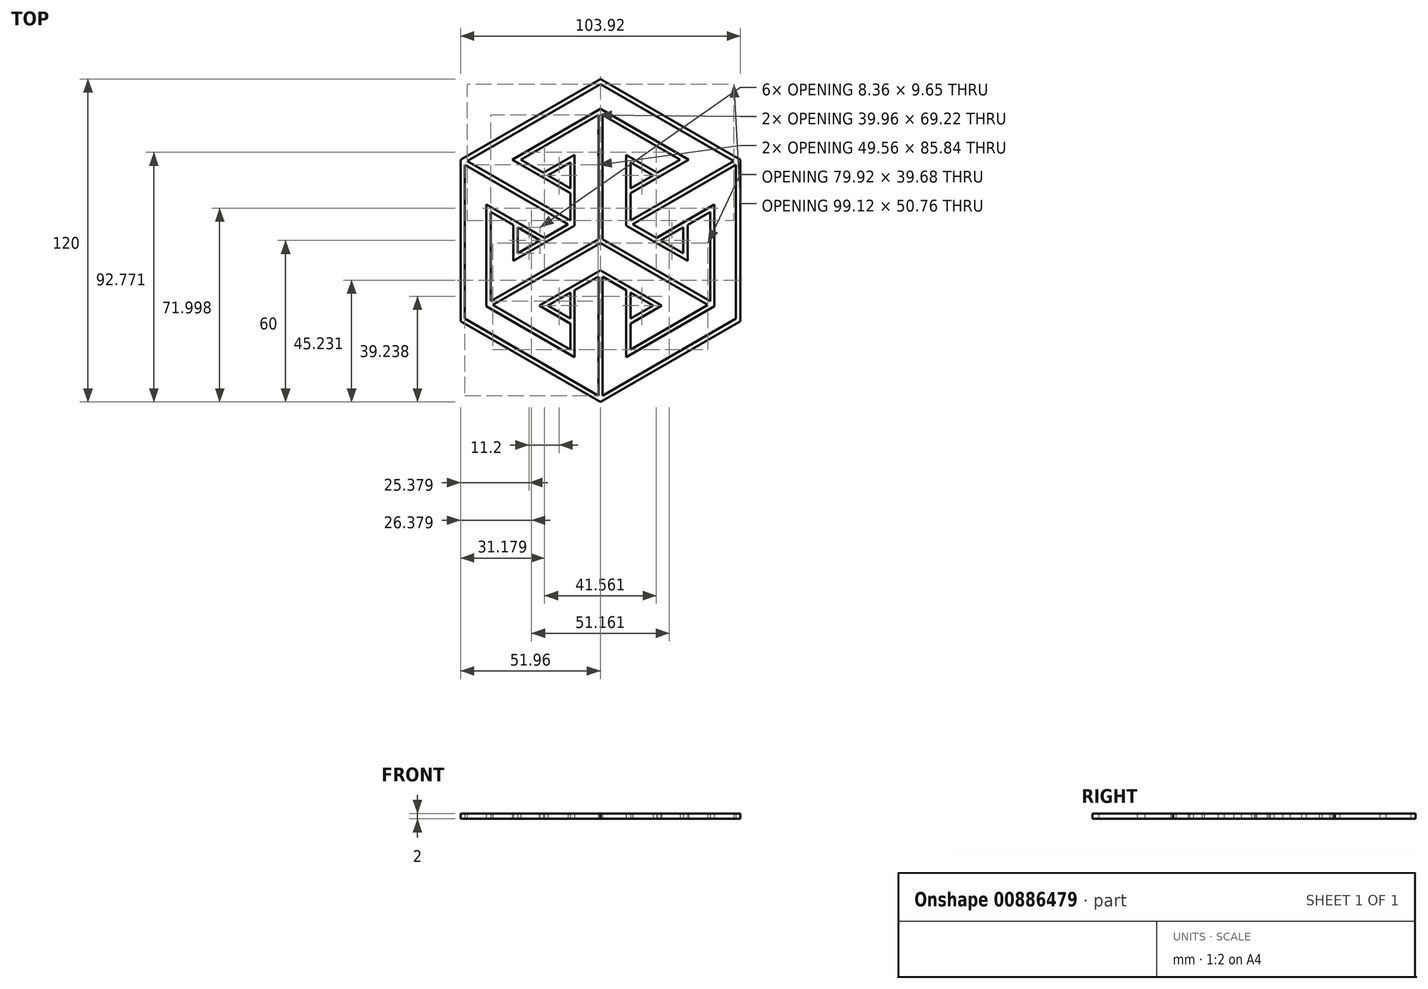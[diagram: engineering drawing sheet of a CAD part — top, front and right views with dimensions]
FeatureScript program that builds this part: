
annotation { "Feature Type Name" : "Feature", "Feature Type Description" : "" }
export const myFeature = defineFeature(function(context is Context, id is Id, definition is map)
    precondition{}
    {
        {
            var Q0;
            Q0=qCreatedBy(makeId("Top.planeOp"),FACE);
            var sketch = newSketch(context, id + "F0", { "sketchPlane" : qUnion([Q0])});
            skLineSegment(sketch, "E0", {"start": v(-51.96, 30) * mm, "end": v(-51.96, -30) * mm});
            skLineSegment(sketch, "E1", {"start": v(-51.96, -30) * mm, "end": v(0, 0) * mm, "construction": true});
            skLineSegment(sketch, "E2", {"start": v(-51.96, 30) * mm, "end": v(0, 0) * mm, "construction": true});
            skLineSegment(sketch, "E3.0", {"start": v(-50.36, 28.15) * mm, "end": v(-50.36, -29.08) * mm});
            skLineSegment(sketch, "E4.trimOffspring", {"start": v(-50.36, 28.15) * mm, "end": v(-12, 6) * mm});
            skLineSegment(sketch, "E5.0", {"start": v(-42.36, 13.37) * mm, "end": v(-20.8, 0.92) * mm});
            skLineSegment(sketch, "E5.1", {"start": v(-42.36, 13.37) * mm, "end": v(-42.36, -24.46) * mm});
            skLineSegment(sketch, "E6.0", {"start": v(-40.76, 10.6) * mm, "end": v(-32.36, 5.75) * mm});
            skLineSegment(sketch, "E6.1", {"start": v(-40.76, 10.6) * mm, "end": v(-40.76, -22.6) * mm});
            skLineSegment(sketch, "E7.0", {"start": v(-30.76, -4.83) * mm, "end": v(-30.76, 4.83) * mm});
            skLineSegment(sketch, "E7.1", {"start": v(-12, 6) * mm, "end": v(-20.8, 0.92) * mm});
            skLineSegment(sketch, "E8.0", {"start": v(-32.36, -7.6) * mm, "end": v(-32.36, 5.75) * mm});
            skLineSegment(sketch, "E8.1", {"start": v(-9.6, 5.54) * mm, "end": v(-32.36, -7.6) * mm});
            skLineSegment(sketch, "E9.trimOffspring", {"start": v(-30.76, 4.83) * mm, "end": v(-22.4, 0) * mm});
            skLineSegment(sketch, "E10.trimOffspring", {"start": v(-22.4, 0) * mm, "end": v(-30.76, -4.83) * mm});
            skLineSegment(sketch, "E11.trimOffspring", {"start": v(-40.76, -22.6) * mm, "end": v(-0.8, 0.46) * mm});
            skLineSegment(sketch, "E12.MirrorCS", {"start": v(-22.76, -24.23) * mm, "end": v(-11.2, -30.9) * mm});
            skLineSegment(sketch, "E13.MirrorCS", {"start": v(-0.8, -57.7) * mm, "end": v(-50.36, -29.08) * mm});
            skLineSegment(sketch, "E14.MirrorCS", {"start": v(-11.2, -40.6) * mm, "end": v(-39.96, -24) * mm});
            skLineSegment(sketch, "E15.MirrorCS", {"start": v(-11.2, -29.05) * mm, "end": v(-11.2, -19.4) * mm});
            skLineSegment(sketch, "E16.MirrorCS", {"start": v(-0.8, -57.7) * mm, "end": v(-0.8, -13.4) * mm});
            skLineSegment(sketch, "E17.MirrorCS", {"start": v(-39.96, -24) * mm, "end": v(0, -0.92) * mm});
            skLineSegment(sketch, "E18.MirrorCS", {"start": v(-19.56, -24.23) * mm, "end": v(-11.2, -29.05) * mm});
            skLineSegment(sketch, "E19.MirrorCS", {"start": v(-11.2, -40.6) * mm, "end": v(-11.2, -30.9) * mm});
            skLineSegment(sketch, "E20.MirrorCS", {"start": v(-9.6, -43.37) * mm, "end": v(-9.6, -18.48) * mm});
            skLineSegment(sketch, "E21.MirrorCS", {"start": v(-9.6, -43.37) * mm, "end": v(-42.36, -24.46) * mm});
            skLineSegment(sketch, "E22.MirrorCS", {"start": v(0, -60) * mm, "end": v(-51.96, -30) * mm});
            skLineSegment(sketch, "E23.MirrorCS", {"start": v(-11.2, -19.4) * mm, "end": v(-19.56, -24.23) * mm});
            skLineSegment(sketch, "E24.MirrorCS", {"start": v(0, -11.09) * mm, "end": v(-22.76, -24.23) * mm});
            skLineSegment(sketch, "E25.MirrorCS", {"start": v(-0.8, -13.4) * mm, "end": v(-9.6, -18.48) * mm});
            skLineSegment(sketch, "E26.MirrorCS", {"start": v(-32.76, 30) * mm, "end": v(0, 48.91) * mm});
            skLineSegment(sketch, "E27.MirrorCS", {"start": v(29.56, 30) * mm, "end": v(0.8, 46.6) * mm});
            skLineSegment(sketch, "E28.MirrorCS", {"start": v(11.2, 19.4) * mm, "end": v(11.2, 29.05) * mm});
            skLineSegment(sketch, "E29.MirrorCS", {"start": v(-9.6, 31.83) * mm, "end": v(-21.16, 25.15) * mm});
            skLineSegment(sketch, "E30.MirrorCS", {"start": v(-49.56, 29.54) * mm, "end": v(0, 58.15) * mm});
            skLineSegment(sketch, "E31.MirrorCS", {"start": v(-11.2, 19.4) * mm, "end": v(-11.2, 29.05) * mm});
            skLineSegment(sketch, "E32.MirrorCS", {"start": v(-0.8, 46.6) * mm, "end": v(-0.8, 0.46) * mm});
            skLineSegment(sketch, "E33.MirrorCS", {"start": v(32.76, 30) * mm, "end": v(11.2, 17.55) * mm});
            skLineSegment(sketch, "E34.MirrorCS", {"start": v(-11.2, 29.05) * mm, "end": v(-19.56, 24.23) * mm});
            skLineSegment(sketch, "E35.MirrorCS", {"start": v(-29.56, 30) * mm, "end": v(-21.16, 25.15) * mm});
            skLineSegment(sketch, "E36.MirrorCS", {"start": v(-49.56, 29.54) * mm, "end": v(-11.2, 7.4) * mm});
            skLineSegment(sketch, "E37.MirrorCS", {"start": v(-19.56, 24.23) * mm, "end": v(-11.2, 19.4) * mm});
            skLineSegment(sketch, "E38.MirrorCS", {"start": v(49.56, 29.54) * mm, "end": v(11.2, 7.4) * mm});
            skLineSegment(sketch, "E39.MirrorCS", {"start": v(19.56, 24.23) * mm, "end": v(11.2, 19.4) * mm});
            skLineSegment(sketch, "E40.MirrorCS", {"start": v(-9.6, 5.54) * mm, "end": v(-9.6, 31.83) * mm});
            skLineSegment(sketch, "E41.MirrorCS", {"start": v(29.56, 30) * mm, "end": v(21.16, 25.15) * mm});
            skLineSegment(sketch, "E42.MirrorCS", {"start": v(49.56, 29.54) * mm, "end": v(0, 58.15) * mm});
            skLineSegment(sketch, "E43.MirrorCS", {"start": v(-32.76, 30) * mm, "end": v(-11.2, 17.55) * mm});
            skLineSegment(sketch, "E44.MirrorCS", {"start": v(-51.96, 30) * mm, "end": v(0, 60) * mm});
            skLineSegment(sketch, "E45.MirrorCS", {"start": v(-11.2, 7.4) * mm, "end": v(-11.2, 17.55) * mm});
            skLineSegment(sketch, "E46.MirrorCS", {"start": v(11.2, 7.4) * mm, "end": v(11.2, 17.55) * mm});
            skLineSegment(sketch, "E47.MirrorCS", {"start": v(11.2, 29.05) * mm, "end": v(19.56, 24.23) * mm});
            skLineSegment(sketch, "E48.MirrorCS", {"start": v(32.76, 30) * mm, "end": v(0, 48.91) * mm});
            skLineSegment(sketch, "E49.MirrorCS", {"start": v(-29.56, 30) * mm, "end": v(-0.8, 46.6) * mm});
            skLineSegment(sketch, "E50.MirrorCS", {"start": v(51.96, 30) * mm, "end": v(0, 60) * mm});
            skLineSegment(sketch, "E51.MirrorCS", {"start": v(9.6, 5.54) * mm, "end": v(9.6, 31.83) * mm});
            skLineSegment(sketch, "E52.MirrorCS", {"start": v(9.6, 31.83) * mm, "end": v(21.16, 25.15) * mm});
            skLineSegment(sketch, "E53.MirrorCS", {"start": v(0.8, 46.6) * mm, "end": v(0.8, 0.46) * mm});
            skLineSegment(sketch, "E54.MirrorCS", {"start": v(0, -60) * mm, "end": v(51.96, -30) * mm});
            skLineSegment(sketch, "E55.MirrorCS", {"start": v(0.8, -57.7) * mm, "end": v(50.36, -29.08) * mm});
            skLineSegment(sketch, "E56.MirrorCS", {"start": v(11.2, -40.6) * mm, "end": v(11.2, -30.9) * mm});
            skLineSegment(sketch, "E57.MirrorCS", {"start": v(0.8, -57.7) * mm, "end": v(0.8, -13.4) * mm});
            skLineSegment(sketch, "E58.MirrorCS", {"start": v(9.6, -43.37) * mm, "end": v(42.36, -24.46) * mm});
            skLineSegment(sketch, "E59.MirrorCS", {"start": v(11.2, -40.6) * mm, "end": v(39.96, -24) * mm});
            skLineSegment(sketch, "E60.MirrorCS", {"start": v(22.76, -24.23) * mm, "end": v(11.2, -30.9) * mm});
            skLineSegment(sketch, "E61.MirrorCS", {"start": v(19.56, -24.23) * mm, "end": v(11.2, -29.05) * mm});
            skLineSegment(sketch, "E62.MirrorCS", {"start": v(11.2, -19.4) * mm, "end": v(19.56, -24.23) * mm});
            skLineSegment(sketch, "E63.MirrorCS", {"start": v(11.2, -29.05) * mm, "end": v(11.2, -19.4) * mm});
            skLineSegment(sketch, "E64.MirrorCS", {"start": v(9.6, -43.37) * mm, "end": v(9.6, -18.48) * mm});
            skLineSegment(sketch, "E65.MirrorCS", {"start": v(0.8, -13.4) * mm, "end": v(9.6, -18.48) * mm});
            skLineSegment(sketch, "E66.MirrorCS", {"start": v(0, -11.09) * mm, "end": v(22.76, -24.23) * mm});
            skLineSegment(sketch, "E67.MirrorCS", {"start": v(40.76, -22.6) * mm, "end": v(0.8, 0.46) * mm});
            skLineSegment(sketch, "E68.MirrorCS", {"start": v(39.96, -24) * mm, "end": v(0, -0.92) * mm});
            skLineSegment(sketch, "E69.MirrorCS", {"start": v(12, 6) * mm, "end": v(20.8, 0.92) * mm});
            skLineSegment(sketch, "E70.MirrorCS", {"start": v(9.6, 5.54) * mm, "end": v(32.36, -7.6) * mm});
            skLineSegment(sketch, "E71.MirrorCS", {"start": v(22.4, 0) * mm, "end": v(30.76, -4.83) * mm});
            skLineSegment(sketch, "E72.MirrorCS", {"start": v(30.76, 4.83) * mm, "end": v(22.4, 0) * mm});
            skLineSegment(sketch, "E73.MirrorCS", {"start": v(30.76, -4.83) * mm, "end": v(30.76, 4.83) * mm});
            skLineSegment(sketch, "E74.MirrorCS", {"start": v(32.36, -7.6) * mm, "end": v(32.36, 5.75) * mm});
            skLineSegment(sketch, "E75.MirrorCS", {"start": v(42.36, 13.37) * mm, "end": v(42.36, -24.46) * mm});
            skLineSegment(sketch, "E76.MirrorCS", {"start": v(40.76, 10.6) * mm, "end": v(40.76, -22.6) * mm});
            skLineSegment(sketch, "E77.MirrorCS", {"start": v(40.76, 10.6) * mm, "end": v(32.36, 5.75) * mm});
            skLineSegment(sketch, "E78.MirrorCS", {"start": v(42.36, 13.37) * mm, "end": v(20.8, 0.92) * mm});
            skLineSegment(sketch, "E79.MirrorCS", {"start": v(50.36, 28.15) * mm, "end": v(12, 6) * mm});
            skLineSegment(sketch, "E80.MirrorCS", {"start": v(51.96, 30) * mm, "end": v(51.96, -30) * mm});
            skLineSegment(sketch, "E81.MirrorCS", {"start": v(50.36, 28.15) * mm, "end": v(50.36, -29.08) * mm});
            skSolve(sketch);
        }
        {
            var Q0;
            Q0=makeQuery(id+"F0.imprint","IMPRINT",FACE,{"disambiguationData":[TD([[makeQuery(id+"F0.imprint","IMPRINT",EDGE,{"derivedFrom":sQuery(id+"F0.wireOp",EDGE,"E0")}),1.0]])]});
            extrude(context, id + "F1", {"entities" : qUnion([Q0]), "depth" : 2 * mm, "offsetDistance" : 25 * mm});
        }
    });
